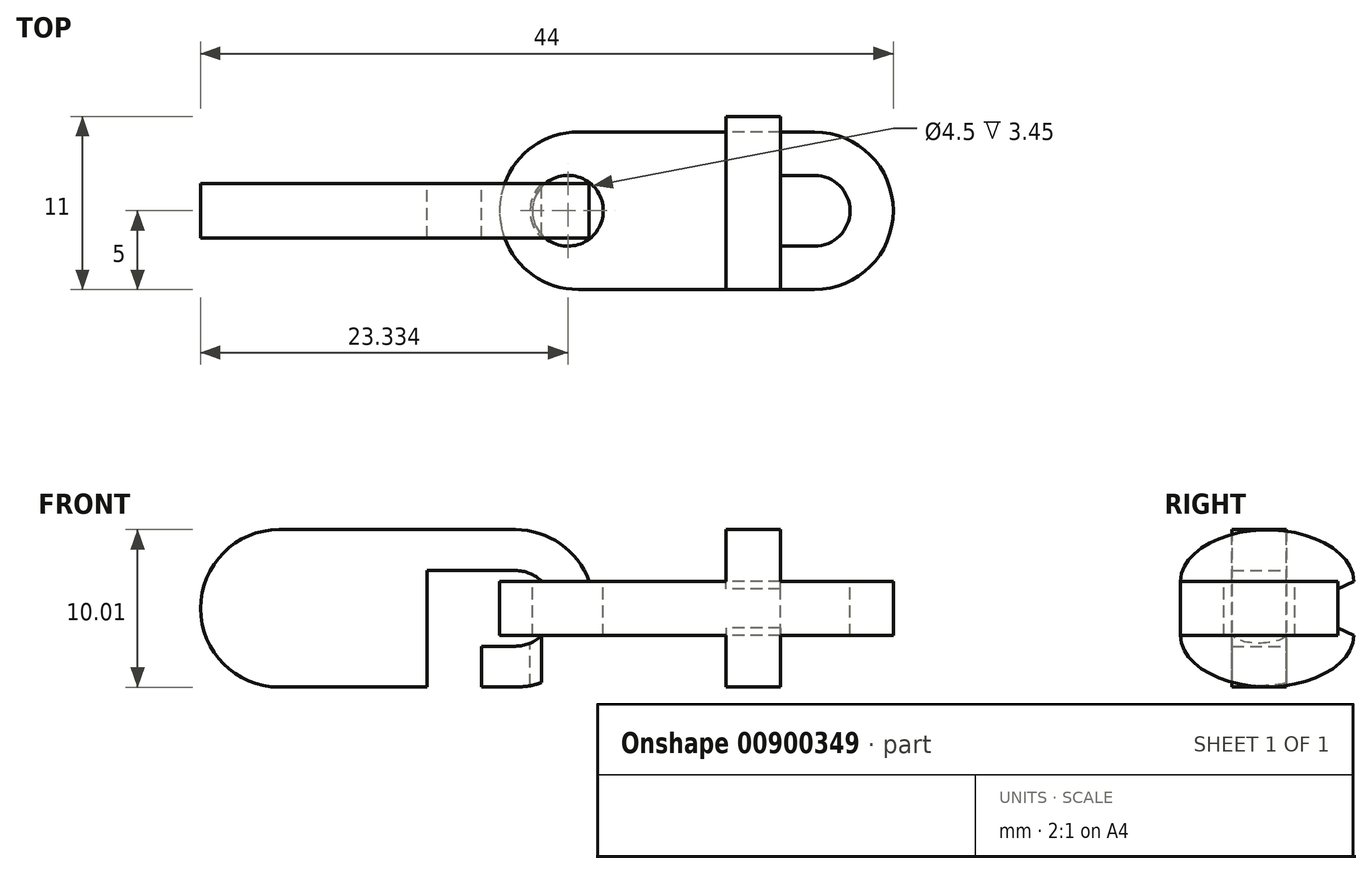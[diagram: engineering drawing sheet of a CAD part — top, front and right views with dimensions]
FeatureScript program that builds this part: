
annotation { "Feature Type Name" : "Feature", "Feature Type Description" : "" }
export const myFeature = defineFeature(function(context is Context, id is Id, definition is map)
    precondition{}
    {
        {
            assignVariable(context, id + "F0", {"name" : "thickness", "anyValue" : 3.45 * mm});
        }
        {
            var Q0;
            Q0=qCreatedBy(makeId("Top.planeOp"),FACE);
            var sketch = newSketch(context, id + "F1", { "sketchPlane" : qUnion([Q0])});
            skArc(sketch, "E0", {"start": v(0, 5) * mm, "mid": v(-5, 0) * mm, "end": v(0, -5) * mm});
            skArc(sketch, "E1", {"start": v(15, -2.4) * mm, "mid": v(17.4, 0) * mm, "end": v(15, 2.4) * mm});
            skLineSegment(sketch, "E2", {"start": v(15, -2.4) * mm, "end": v(15, -5) * mm, "construction": true});
            skArc(sketch, "E3", {"start": v(15, -5) * mm, "mid": v(20, 0) * mm, "end": v(15, 5) * mm});
            skLineSegment(sketch, "E4", {"start": v(15, 5) * mm, "end": v(0, 5) * mm});
            skLineSegment(sketch, "E5", {"start": v(15, 0) * mm, "end": v(19, 0) * mm, "construction": true});
            skLineSegment(sketch, "E6", {"start": v(15, -5) * mm, "end": v(12.84, -5) * mm});
            skLineSegment(sketch, "E7", {"start": v(12.84, -5) * mm, "end": v(9.39, -5) * mm, "construction": true});
            skLineSegment(sketch, "E8", {"start": v(0, -5) * mm, "end": v(9.39, -5) * mm});
            skLineSegment(sketch, "E9", {"start": v(9.39, -5) * mm, "end": v(9.39, 2.4) * mm});
            skLineSegment(sketch, "E10", {"start": v(15, 2.4) * mm, "end": v(9.39, 2.4) * mm});
            skLineSegment(sketch, "E11", {"start": v(15, -2.4) * mm, "end": v(12.84, -2.4) * mm});
            skLineSegment(sketch, "E12", {"start": v(12.84, -2.4) * mm, "end": v(12.84, -5) * mm});
            skSolve(sketch);
        }
        {
            var Q0;
            Q0=makeQuery(id+"F1.imprint","IMPRINT",FACE,{"disambiguationData":[TD([[makeQuery(id+"F1.imprint","IMPRINT",EDGE,{"derivedFrom":sQuery(id+"F1.wireOp",EDGE,"E0")}),1.0]])]});
            extrude(context, id + "F2", {"entities" : qUnion([Q0]), "depth" : getVariable(context, 'thickness'), "offsetDistance" : 25 * mm});
        }
        {
            var Q0;
            Q0=makeQuery(id+"F2.opExtrude","CAP_EDGE",EDGE,{"disambiguationData":[OSD([sQuery(id+"F1.wireOp",EDGE,"E1")])],"isStart":false});
            cPoint(context, id + "F3", {"entities" : qUnion([Q0]), "parameter" : 0.5});
        }
        {
            var Q0;
            Q0=makeQuery(id+"F2.opExtrude","CAP_EDGE",EDGE,{"disambiguationData":[OSD([sQuery(id+"F1.wireOp",EDGE,"E1")])],"isStart":true});
            cPoint(context, id + "F4", {"entities" : qUnion([Q0]), "parameter" : 0.5});
        }
        {
            var Q0;
            Q0=qCreatedBy(makeId("Origin.pointOp"),VERTEX);
            var Q1;
            Q1 = qCreatedBy(id + "F3" ,VERTEX);
            var Q2;
            Q2 = qCreatedBy(id + "F4" ,VERTEX);
            cPlane(context, id + "F5", {"entities" : qUnion([Q0, Q1, Q2]), "cplaneType" : CPlaneType.THREE_POINT, "offset" : 25 * mm, "width" : 150 * mm, "height" : 150 * mm});
        }
        {
            var Q0;
            Q0=qCreatedBy(id+"F5.planeOp",FACE);
            var sketch = newSketch(context, id + "F6", { "sketchPlane" : qUnion([Q0])});
            skPoint(sketch, "E13.0", {"position": v(0, 1.73) * mm});
            skLineSegment(sketch, "E14", {"start": v(0, 1.73) * mm, "end": v(9.39, 1.73) * mm, "construction": true});
            skPoint(sketch, "E15.0", {"position": v(9.39, 1.73) * mm});
            skSolve(sketch);
        }
        {
            var Q0;
            Q0=makeQuery(id+"F2.opExtrude","SWEPT_BODY",BODY,{"disambiguationData":[OSD([sQuery(id+"F1.wireOp",EDGE,"E0"),sQuery(id+"F1.wireOp",EDGE,"kQEwNaL0-Kalx-0nlj-JyWC-PINhUZG8LjUI"),sQuery(id+"F1.wireOp",EDGE,"xpdikLYC-09XZ-7TeU-ZpT2-pXlyAOzpkLWD"),sQuery(id+"F1.wireOp",EDGE,"yWZhYI9k-zFp2-B0rH-yDnl-Vr2n4LNi4M2W"),sQuery(id+"F1.wireOp",EDGE,"E1"),sQuery(id+"F1.wireOp",EDGE,"E2"),sQuery(id+"F1.wireOp",EDGE,"E3"),sQuery(id+"F1.wireOp",EDGE,"E4")])]});
            var Q1;
            Q1=sQuery(id+"F6.wireOp",EDGE,"E14");
            transform(context, id + "F7", {"entities" : qUnion([Q0]), "transformType" : TransformType.ROTATION, "transformAxis" : qUnion([Q1]), "angle" : 90 * degree, "makeCopy" : true});
        }
        {
            var Q0;
            Q0=makeQuery(id+"F7.opPattern","COPY",BODY,{"derivedFrom":makeQuery(id+"F2.opExtrude","SWEPT_BODY",BODY,{"disambiguationData":[OSD([sQuery(id+"F1.wireOp",EDGE,"E0"),sQuery(id+"F1.wireOp",EDGE,"kQEwNaL0-Kalx-0nlj-JyWC-PINhUZG8LjUI"),sQuery(id+"F1.wireOp",EDGE,"xpdikLYC-09XZ-7TeU-ZpT2-pXlyAOzpkLWD"),sQuery(id+"F1.wireOp",EDGE,"yWZhYI9k-zFp2-B0rH-yDnl-Vr2n4LNi4M2W"),sQuery(id+"F1.wireOp",EDGE,"E1"),sQuery(id+"F1.wireOp",EDGE,"E2"),sQuery(id+"F1.wireOp",EDGE,"E3"),sQuery(id+"F1.wireOp",EDGE,"E4")])]}),"instanceName":"1"});
            transform(context, id + "F8", {"entities" : qUnion([Q0]), "transformType" : TransformType.TRANSLATION_3D, "dx" : -19 * mm, "dy" : 0 * mm, "dz" : 0 * mm, "makeCopy" : false});
        }
        {
            var Q0;
            Q0=makeQuery(id+"F2.opExtrude","CAP_FACE",FACE,{"disambiguationData":[OSD([sQuery(id+"F1.wireOp",EDGE,"E0"),sQuery(id+"F1.wireOp",EDGE,"kQEwNaL0-Kalx-0nlj-JyWC-PINhUZG8LjUI"),sQuery(id+"F1.wireOp",EDGE,"xpdikLYC-09XZ-7TeU-ZpT2-pXlyAOzpkLWD"),sQuery(id+"F1.wireOp",EDGE,"yWZhYI9k-zFp2-B0rH-yDnl-Vr2n4LNi4M2W"),sQuery(id+"F1.wireOp",EDGE,"E1"),sQuery(id+"F1.wireOp",EDGE,"E2"),sQuery(id+"F1.wireOp",EDGE,"E3"),sQuery(id+"F1.wireOp",EDGE,"E4")])],"isStart":false});
            var sketch = newSketch(context, id + "F9", { "sketchPlane" : qUnion([Q0])});
            skLineSegment(sketch, "E16", {"start": v(-2.33, 1.72) * mm, "end": v(-2.33, -1.72) * mm, "construction": true});
            skPoint(sketch, "E17.0", {"position": v(1, -1.72) * mm});
            skPoint(sketch, "E17.1", {"position": v(1, 1.73) * mm});
            skLineSegment(sketch, "E18", {"start": v(-2.33, 1.73) * mm, "end": v(1, -1.72) * mm, "construction": true});
            skCircle(sketch, "E19", {"center": v(-0.67, 0) * mm, "radius": 2.4 * mm});
            skSolve(sketch);
        }
        {
            var Q0;
            Q0=makeQuery(id+"F9.imprint","IMPRINT",FACE,{"disambiguationData":[TD([[makeQuery(id+"F9.imprint","IMPRINT",EDGE,{"derivedFrom":sQuery(id+"F9.wireOp",EDGE,"E19")}),1.0]])]});
            extrude(context, id + "F10", {"entities" : qUnion([Q0]), "operationType" : NewBodyOperationType.REMOVE, "endBound" : BoundingType.THROUGH_ALL, "oppositeDirection" : true, "depth" : 25 * mm, "offsetDistance" : 25 * mm});
        }
        {
            var Q0;
            Q0=makeQuery(id+"F2.opExtrude","SWEPT_FACE",FACE,{"disambiguationData":[OSD([sQuery(id+"F1.wireOp",EDGE,"E9")])]});
            var sketch = newSketch(context, id + "F11", { "sketchPlane" : qUnion([Q0])});
            skFitSpline(sketch, "E20", {"points": [v(-5, 3.45) * mm, v(0.5, 6.72) * mm, v(6, 3.45) * mm], "startDerivative": vector(0, 11.3) * mm, "endDerivative": vector(0, -11.3) * mm});
            skLineSegment(sketch, "E21", {"start": v(6, 3.45) * mm, "end": v(0.5, 6.72) * mm, "construction": true});
            skLineSegment(sketch, "E22", {"start": v(-5, 3.45) * mm, "end": v(0.5, 6.72) * mm, "construction": true});
            skLineSegment(sketch, "E23", {"start": v(5, 3.45) * mm, "end": v(5, 0) * mm, "construction": true});
            skLineSegment(sketch, "E24.0", {"start": v(-1.72, 6.72) * mm, "end": v(1.73, 6.72) * mm, "construction": true});
            skLineSegment(sketch, "E25", {"start": v(6, 3.45) * mm, "end": v(5, 2.95) * mm});
            skLineSegment(sketch, "E26", {"start": v(5, 2.95) * mm, "end": v(5, 3.45) * mm});
            skLineSegment(sketch, "E27", {"start": v(5, 3.45) * mm, "end": v(2.4, 3.45) * mm});
            skLineSegment(sketch, "E28", {"start": v(2.4, 3.45) * mm, "end": v(2.4, 1.73) * mm});
            skLineSegment(sketch, "E29", {"start": v(2.4, 1.73) * mm, "end": v(-5, 1.73) * mm, "construction": true});
            skLineSegment(sketch, "E30", {"start": v(-5, 1.73) * mm, "end": v(-5, 3.45) * mm});
            skLineSegment(sketch, "E31.MirrorCS", {"start": v(2.4, 0) * mm, "end": v(2.4, 1.73) * mm});
            skLineSegment(sketch, "E32.MirrorCS", {"start": v(5, 0) * mm, "end": v(2.4, 0) * mm});
            skLineSegment(sketch, "E33.MirrorCS", {"start": v(5, 0.5) * mm, "end": v(5, 0) * mm});
            skLineSegment(sketch, "E34.MirrorCS", {"start": v(-5, 1.73) * mm, "end": v(-5, 0) * mm});
            skLineSegment(sketch, "E35.MirrorCS", {"start": v(6, 0) * mm, "end": v(5, 0.5) * mm});
            skFitSpline(sketch, "E36.MirrorCS", {"points": [v(-5, 0) * mm, v(0.5, -3.27) * mm, v(6, 0) * mm], "startDerivative": vector(0, -11.3) * mm, "endDerivative": vector(0, 11.3) * mm});
            skSolve(sketch);
        }
        {
            var Q0;
            Q0 = qSketchRegion(id + "F11", true);
            extrude(context, id + "F12", {"entities" : qUnion([Q0]), "depth" : getVariable(context, 'thickness'), "offsetDistance" : 25 * mm});
        }
        {
            var Q0;
            Q0=makeQuery(id+"F2.opExtrude","CAP_FACE",FACE,{"disambiguationData":[OSD([sQuery(id+"F1.wireOp",EDGE,"E0"),sQuery(id+"F1.wireOp",EDGE,"E1"),sQuery(id+"F1.wireOp",EDGE,"E3"),sQuery(id+"F1.wireOp",EDGE,"E4"),sQuery(id+"F1.wireOp",EDGE,"E6"),sQuery(id+"F1.wireOp",EDGE,"E8"),sQuery(id+"F1.wireOp",EDGE,"E9"),sQuery(id+"F1.wireOp",EDGE,"E10"),sQuery(id+"F1.wireOp",EDGE,"E11"),sQuery(id+"F1.wireOp",EDGE,"E12")])],"isStart":false});
            var sketch = newSketch(context, id + "F13", { "sketchPlane" : qUnion([Q0])});
            skCircle(sketch, "E37.0", {"center": v(-0.67, 0) * mm, "radius": 2.25 * mm});
            skLineSegment(sketch, "E38.0", {"start": v(15, -2.25) * mm, "end": v(12.84, -2.25) * mm});
            skArc(sketch, "E38.1", {"start": v(15, -2.25) * mm, "mid": v(17.25, 0) * mm, "end": v(15, 2.25) * mm});
            skLineSegment(sketch, "E38.2", {"start": v(15, 2.25) * mm, "end": v(9.39, 2.25) * mm});
            skLineSegment(sketch, "E39", {"start": v(12.84, -2.25) * mm, "end": v(12.84, -2.4) * mm});
            skSolve(sketch);
        }
        {
            var Q0;
            Q0=makeQuery(id+"F13.imprint","IMPRINT",FACE,{"disambiguationData":[TD([[makeQuery(id+"F13.imprint","IMPRINT",EDGE,{"derivedFrom":sQuery(id+"F13.wireOp",EDGE,"E37.0")}),-1.0]])]});
            var Q1;
            Q1=makeQuery(id+"F13.imprint","IMPRINT",FACE,{"disambiguationData":[TD([[makeQuery(id+"F13.imprint","IMPRINT",EDGE,{"derivedFrom":sQuery(id+"F13.wireOp",EDGE,"E38.0")}),1.0]])]});
            var Q2;
            Q2=makeQuery(id+"F2.opExtrude","CAP_FACE",FACE,{"disambiguationData":[OSD([sQuery(id+"F1.wireOp",EDGE,"E0"),sQuery(id+"F1.wireOp",EDGE,"E1"),sQuery(id+"F1.wireOp",EDGE,"E3"),sQuery(id+"F1.wireOp",EDGE,"E4"),sQuery(id+"F1.wireOp",EDGE,"E6"),sQuery(id+"F1.wireOp",EDGE,"E8"),sQuery(id+"F1.wireOp",EDGE,"E9"),sQuery(id+"F1.wireOp",EDGE,"E10"),sQuery(id+"F1.wireOp",EDGE,"E11"),sQuery(id+"F1.wireOp",EDGE,"E12")])],"isStart":true});
            extrude(context, id + "F14", {"entities" : qUnion([Q0, Q1]), "operationType" : NewBodyOperationType.ADD, "endBound" : BoundingType.UP_TO_SURFACE, "oppositeDirection" : true, "depth" : 25 * mm, "endBoundEntityFace" : qUnion([Q2]), "offsetDistance" : 25 * mm});
        }
    });
